# Revit family: НЕВАТОМ_Козырек защитный VO, версия 1
name_source: partatom
category: Оборудование
revit_build: Autodesk Revit 2017 (Build: 20170118_1100(x64)
units: mm (PartAtom-declared; Revit-internal decimal feet)

## family parameters
Всегда вертикально = Нет
На основе рабочей плоскости = Да
Общий = Нет
При загрузке вырезать с полостями = Нет
Размер круглого соединителя = Использовать диаметр
Тип детали = Нормальный
Точка расчета площади = Нет

## types (10) — shared parameters
ADSK_Единица измерения = шт.
ADSK_Завод-изготовитель = NEVATOM
ADSK_Материал наименование = сталь оцинкованная
Nevatom_URL = https://t.me
Отметка по умолчанию = 1219 мм
рамка = 50 мм
расстояние решетки = 10 мм
угол вырезания = 29.00°
шаг = 50 мм
ширина до среза = 50 мм

## per-type parameters (varying)
| type | ADSK_Марка | ADSK_Масса | D | D+10 | Dнф | L | а | вырез ширина |
| Козырек защитный VO № 16,0 | VO № 16,0 | 71.58 | 1600 мм | 1610 мм | 1680 мм | 975 мм | 3119 мм | 1650 мм |
| Козырек защитный VO № 4,0 | VO № 4,0 | 3.54 | 400 мм | 410 мм | 450 мм | 283 мм | 3119 мм | 450 мм |
| Козырек защитный VO № 4,5 | VO № 4,5 | 4.23 | 450 мм | 460 мм | 500 мм | 312 мм | 3119 мм | 500 мм |
| Козырек защитный VO № 5,0 | VO № 5,0 | 4.71 | 500 мм | 510 мм | 550 мм | 326 мм | 3119 мм | 550 мм |
| Козырек защитный VO № 5,6 | VO № 5,6 | 5.71 | 560 мм | 570 мм | 610 мм | 375 мм | 2000 мм | 610 мм |
| Козырек защитный VO № 7,1 | VO № 7,1 | 12.11 | 710 мм | 720 мм | 790 мм | 461 мм | 2000 мм | 760 мм |
| Козырек защитный VO № 8,0 | VO № 8,0 | 14 | 800 мм | 810 мм | 864 мм | 513 мм | 2000 мм | 850 мм |
| Козырек защитный VO № 11,2 | VO № 11,2 | 35.22 | 1120 мм | 1130 мм | 1184 мм | 697 мм | 2000 мм | 1170 мм |
| Козырек защитный VO № 12,5 | VO № 12,5 | 44 | 1250 мм | 1260 мм | 1330 мм | 773 мм | 2000 мм | 1300 мм |
| Козырек защитный VO № 14,0 | VO № 14,0 | 53.79 | 1400 мм | 1410 мм | 1480 мм | 860 мм | 2000 мм | 1450 мм |

note: column(s) folded — value = type name in every type: ADSK_Наименование
